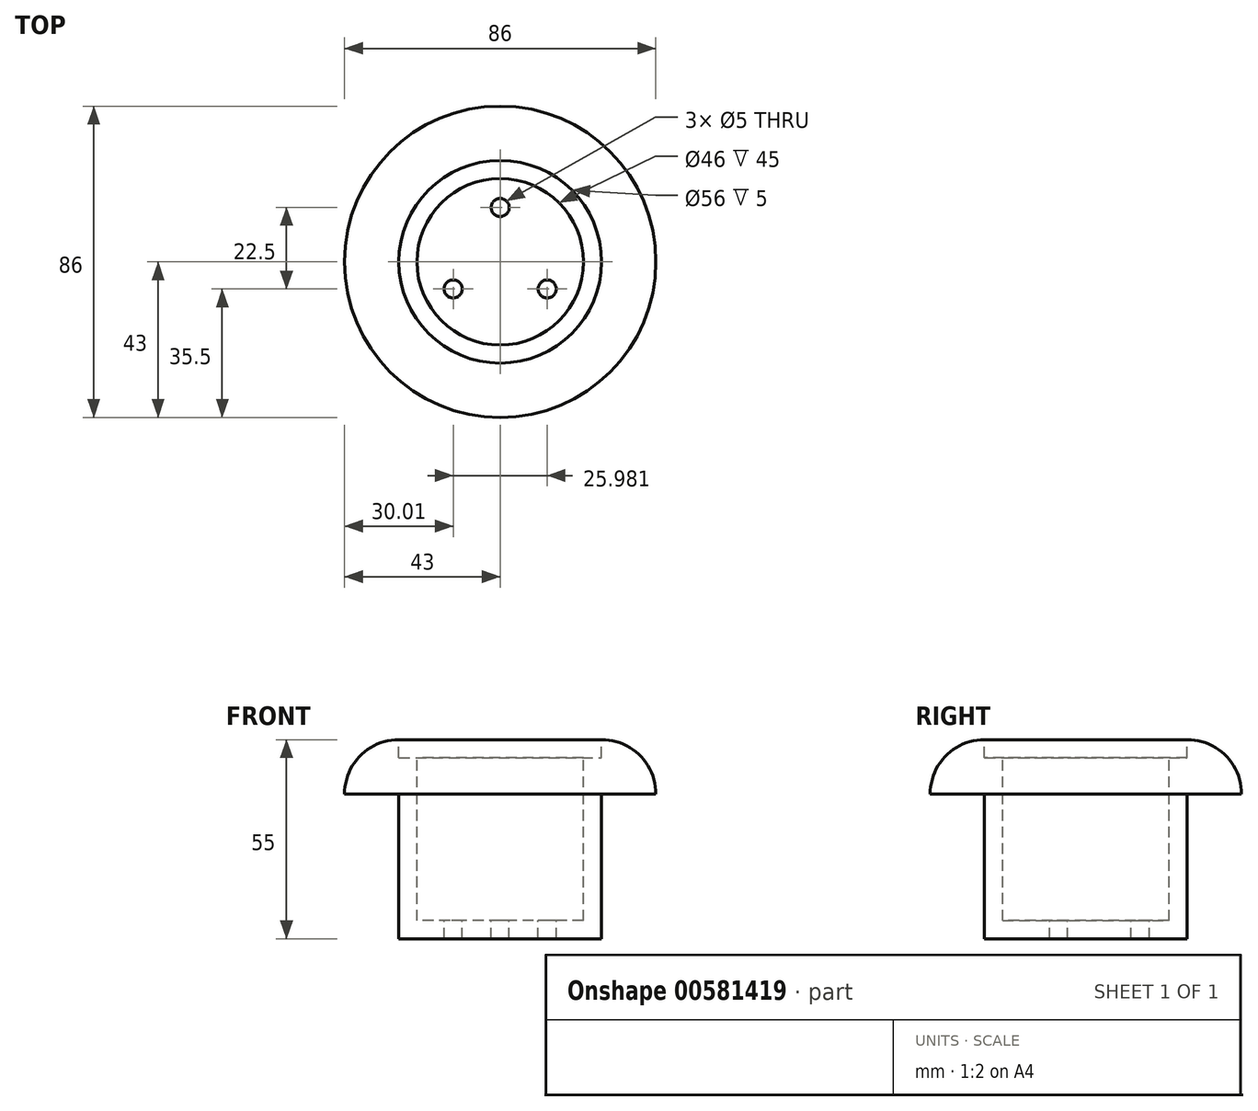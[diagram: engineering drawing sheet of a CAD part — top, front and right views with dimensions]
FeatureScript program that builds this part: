
annotation { "Feature Type Name" : "Feature", "Feature Type Description" : "" }
export const myFeature = defineFeature(function(context is Context, id is Id, definition is map)
    precondition{}
    {
        {
            var Q0;
            Q0=qCreatedBy(makeId("Front.planeOp"),FACE);
            var sketch = newSketch(context, id + "F0", { "sketchPlane" : qUnion([Q0])});
            skLineSegment(sketch, "E0", {"start": v(43, 30) * mm, "end": v(43, 15) * mm});
            skLineSegment(sketch, "E1", {"start": v(43, 15) * mm, "end": v(28, 15) * mm});
            skLineSegment(sketch, "E2", {"start": v(28, 15) * mm, "end": v(28, -15) * mm});
            skLineSegment(sketch, "E3", {"start": v(43, 30) * mm, "end": v(23, 30) * mm});
            skLineSegment(sketch, "E4", {"start": v(23, 30) * mm, "end": v(23, -20) * mm});
            skLineSegment(sketch, "E5", {"start": v(23, -20) * mm, "end": v(0, -20) * mm});
            skLineSegment(sketch, "E6", {"start": v(0, -25) * mm, "end": v(28, -25) * mm});
            skLineSegment(sketch, "E7", {"start": v(28, -25) * mm, "end": v(28, -15) * mm});
            skLineSegment(sketch, "E8", {"start": v(0, -20) * mm, "end": v(0, -25) * mm});
            skSolve(sketch);
        }
        {
            var Q0;
            Q0=makeQuery(id+"F0.imprint","IMPRINT",FACE,{"disambiguationData":[TD([[makeQuery(id+"F0.imprint","IMPRINT",EDGE,{"derivedFrom":sQuery(id+"F0.wireOp",EDGE,"E0")}),-1.0]])]});
            var Q1;
            Q1=sQuery(id+"F0.wireOp",EDGE,"E8");
            revolve(context, id + "F1", {"entities" : qUnion([Q0]), "axis" : qUnion([Q1]), "revolveType" : RevolveType.FULL});
        }
        {
            var Q0;
            Q0=makeQuery(id+"F1.opRevolve","SWEPT_EDGE",EDGE,{"disambiguationData":[OSD([sQuery(id+"F0.wireOp",EDGE,"E0"),sQuery(id+"F0.wireOp",EDGE,"E3")])]});
            fillet(context, id + "F2", {"entities" : qUnion([Q0]), "radius" : 15 * mm, "tangentPropagation" : true, "allowEdgeOverflow" : false});
        }
        {
            var Q0;
            Q0=makeQuery(id+"F1.opRevolve","SWEPT_FACE",FACE,{"disambiguationData":[OSD([sQuery(id+"F0.wireOp",EDGE,"E5")])]});
            var sketch = newSketch(context, id + "F3", { "sketchPlane" : qUnion([Q0])});
            skPoint(sketch, "E9", {"position": v(0, 15) * mm});
            skPoint(sketch, "E10.1.0", {"position": v(-13, -7.5) * mm});
            skPoint(sketch, "E10.2.0", {"position": v(13, -7.5) * mm});
            skPoint(sketch, "E10.center", {"position": v(0, 0) * mm});
            skSolve(sketch);
        }
        {
            var Q0;
            Q0=sQuery(id+"F3.wireOp",VERTEX,"E9");
            var Q1;
            Q1=sQuery(id+"F3.wireOp",VERTEX,"E10.1.0");
            var Q2;
            Q2=sQuery(id+"F3.wireOp",VERTEX,"E10.2.0");
            var Q3;
            Q3=makeQuery(id+"F1.opRevolve","SWEPT_BODY",BODY,{"disambiguationData":[OSD([sQuery(id+"F0.wireOp",EDGE,"E0"),sQuery(id+"F0.wireOp",EDGE,"E1"),sQuery(id+"F0.wireOp",EDGE,"E2"),sQuery(id+"F0.wireOp",EDGE,"E3"),sQuery(id+"F0.wireOp",EDGE,"E4"),sQuery(id+"F0.wireOp",EDGE,"E5"),sQuery(id+"F0.wireOp",EDGE,"E6"),sQuery(id+"F0.wireOp",EDGE,"E7"),sQuery(id+"F0.wireOp",EDGE,"E8")])]});
            hole(context, id + "F4", {"style" : HoleStyle.SIMPLE, "endStyle" : HoleEndStyle.THROUGH, "holeDiameter" : 5 * mm, "majorDiameter" : 5 * mm, "isTappedThrough" : true, "tappedDepth" : 12 * mm, "tapClearance" : 3, "locations" : qUnion([Q0, Q1, Q2]), "scope" : qUnion([Q3])});
        }
        {
            var Q0;
            Q0=makeQuery(id+"F1.opRevolve","SWEPT_FACE",FACE,{"disambiguationData":[OSD([sQuery(id+"F0.wireOp",EDGE,"E3")])]});
            var sketch = newSketch(context, id + "F5", { "sketchPlane" : qUnion([Q0])});
            skLineSegment(sketch, "E11", {"start": v(0, 0) * mm, "end": v(28, 0) * mm});
            skCircle(sketch, "E12", {"center": v(0, 0) * mm, "radius": 28 * mm});
            skSolve(sketch);
        }
        {
            var Q0;
            Q0=makeQuery(id+"F5.imprint","IMPRINT",FACE,{"disambiguationData":[TD([[makeQuery(id+"F5.imprint","IMPRINT",EDGE,{"derivedFrom":sQuery(id+"F5.wireOp",EDGE,"E12")}),1.0]])]});
            extrude(context, id + "F6", {"entities" : qUnion([Q0]), "operationType" : NewBodyOperationType.REMOVE, "oppositeDirection" : true, "depth" : 5 * mm, "offsetDistance" : 25 * mm});
        }
    });
